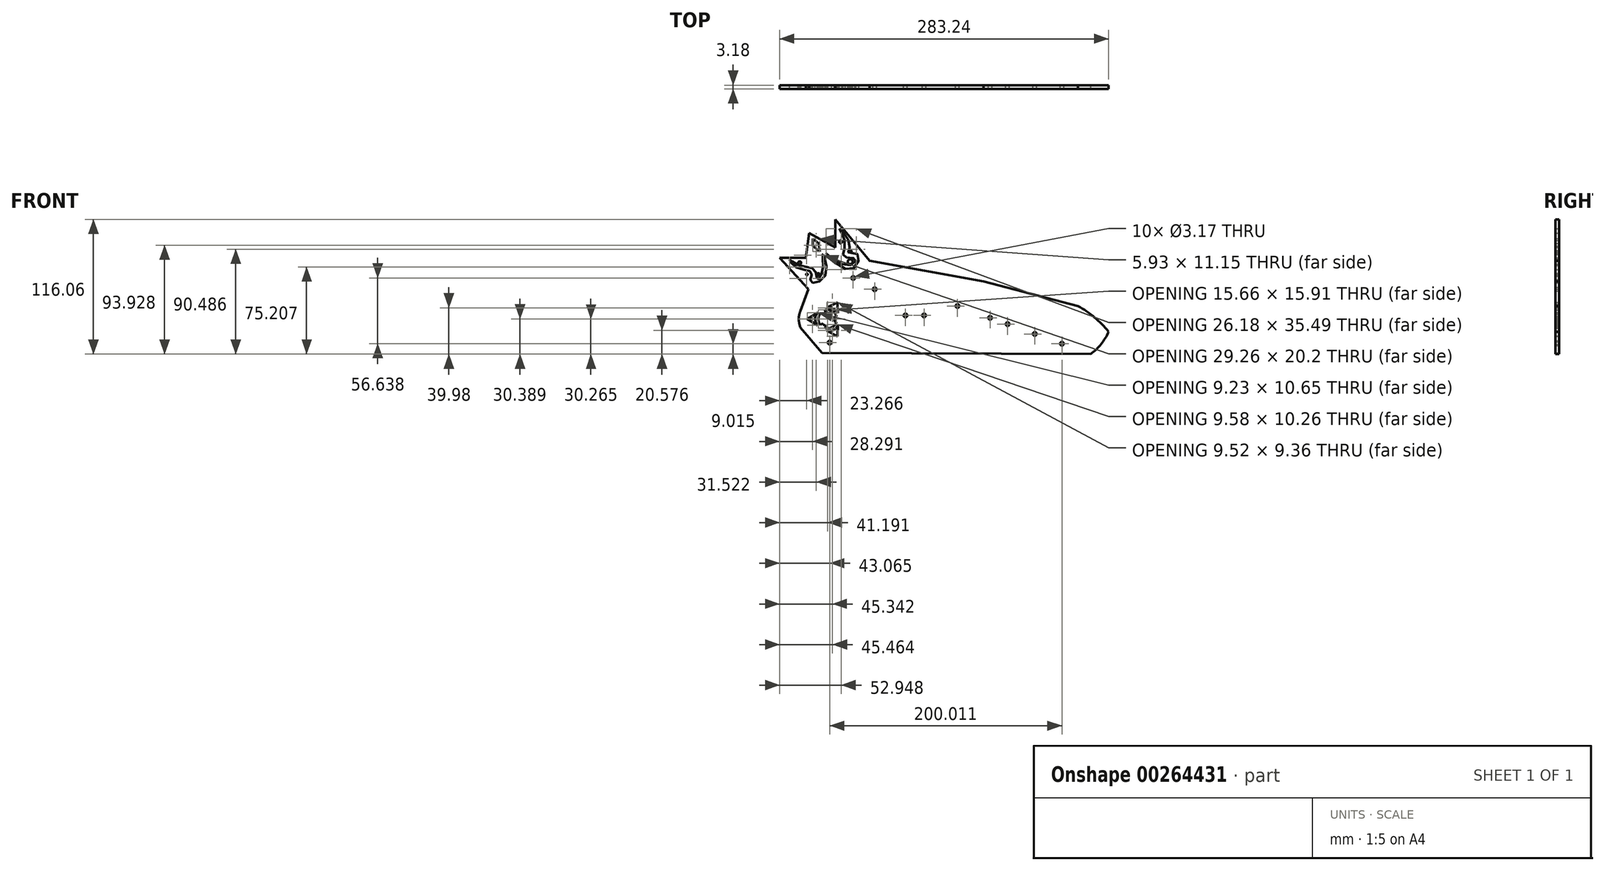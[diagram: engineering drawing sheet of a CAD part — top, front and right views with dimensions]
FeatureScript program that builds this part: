
annotation { "Feature Type Name" : "Feature", "Feature Type Description" : "" }
export const myFeature = defineFeature(function(context is Context, id is Id, definition is map)
    precondition{}
    {
        {
            var Q0;
            Q0=qCreatedBy(makeId("Front.planeOp"),FACE);
            var sketch = newSketch(context, id + "F0", { "sketchPlane" : qUnion([Q0])});
            skCircle(sketch, "E0", {"center": v(-42.49, 14.48) * mm, "radius": 1.59 * mm});
            skCircle(sketch, "E1", {"center": v(-16.03, -8.08) * mm, "radius": 1.59 * mm});
            skLineSegment(sketch, "E2", {"start": v(-99.75, 14.6) * mm, "end": v(-124.36, 41.72) * mm});
            skLineSegment(sketch, "E3", {"start": v(-124.36, 41.72) * mm, "end": v(-101.86, 41.72) * mm});
            skLineSegment(sketch, "E4", {"start": v(-47.04, 39.02) * mm, "end": v(-76.5, 74.6) * mm});
            skLineSegment(sketch, "E5", {"start": v(-76.5, 74.6) * mm, "end": v(-76.5, 50.6) * mm});
            skLineSegment(sketch, "E6", {"start": v(-76.5, 50.6) * mm, "end": v(-98.93, 62.93) * mm});
            skLineSegment(sketch, "E7", {"start": v(-101.86, 41.72) * mm, "end": v(-98.93, 62.93) * mm});
            skPoint(sketch, "E8.visualSharp", {"position": v(-110.59, 3.4) * mm});
            skPoint(sketch, "E9.visualSharp", {"position": v(-87.71, -40.32) * mm});
            skCircle(sketch, "E10", {"center": v(-61.03, 24.2) * mm, "radius": 1.59 * mm});
            skPoint(sketch, "E11.0.midPoint", {"position": v(-90.91, 8.24) * mm});
            skPoint(sketch, "E12.orphan", {"position": v(-121.05, -10.33) * mm});
            skCircle(sketch, "E13", {"center": v(0, -8.08) * mm, "radius": 1.59 * mm});
            skCircle(sketch, "E14", {"center": v(28.76, 0) * mm, "radius": 1.59 * mm});
            skCircle(sketch, "E15", {"center": v(56.86, -10.13) * mm, "radius": 1.59 * mm});
            skCircle(sketch, "E16", {"center": v(71.93, -15.57) * mm, "radius": 1.59 * mm});
            skCircle(sketch, "E17", {"center": v(95.32, -24) * mm, "radius": 1.59 * mm});
            skCircle(sketch, "E18", {"center": v(118.72, -32.44) * mm, "radius": 1.59 * mm});
            skLineSegment(sketch, "E19", {"start": v(143.47, -41.46) * mm, "end": v(-87.71, -40.32) * mm});
            skArc(sketch, "E20", {"start": v(143.47, -41.46) * mm, "mid": v(152.46, -32.83) * mm, "end": v(158.88, -22.16) * mm});
            skArc(sketch, "E21", {"start": v(158.88, -22.16) * mm, "mid": v(146.83, -9.72) * mm, "end": v(132.5, 0) * mm});
            skLineSegment(sketch, "E22", {"start": v(-47.04, 39.02) * mm, "end": v(51.06, 21.22) * mm});
            skLineSegment(sketch, "E23", {"start": v(51.06, 21.22) * mm, "end": v(132.5, 0) * mm});
            skLineSegment(sketch, "E24", {"start": v(-87.71, -40.32) * mm, "end": v(-106.44, -18.45) * mm});
            skLineSegment(sketch, "E25", {"start": v(-106.63, -4.43) * mm, "end": v(-99.75, 14.6) * mm});
            skArc(sketch, "E26", {"start": v(-106.63, -4.43) * mm, "mid": v(-107.82, -11.46) * mm, "end": v(-106.44, -18.45) * mm});
            skLineSegment(sketch, "E27", {"start": v(-89.87, 46.9) * mm, "end": v(-90.77, 53.82) * mm});
            skLineSegment(sketch, "E28", {"start": v(-90.77, 53.82) * mm, "end": v(-95.8, 58.04) * mm});
            skLineSegment(sketch, "E29", {"start": v(-95.8, 58.04) * mm, "end": v(-95.8, 51.75) * mm});
            skLineSegment(sketch, "E30", {"start": v(-95.8, 51.75) * mm, "end": v(-89.87, 46.9) * mm});
            skFitSpline(sketch, "E31", {"points": [v(-115.72, 39.86) * mm, v(-109.85, 33.31) * mm, v(-96.92, 28.78) * mm, v(-97.59, 21.05) * mm, v(-85.33, 25.59) * mm, v(-87.17, 44.57) * mm, v(-87.34, 31.13) * mm, v(-91.88, 23.07) * mm, v(-94.06, 30.8) * mm, v(-109.34, 35.67) * mm, v(-115.72, 39.86) * mm]});
            skFitSpline(sketch, "E32", {"points": [v(-73, 66.77) * mm, v(-63.9, 53.25) * mm, v(-65.05, 45.99) * mm, v(-57.07, 44.37) * mm, v(-63.76, 31.3) * mm, v(-84.6, 45.46) * mm, v(-66.63, 34.87) * mm, v(-58.95, 40.37) * mm, v(-69.16, 42.87) * mm, v(-67.99, 54.65) * mm, v(-73, 66.77) * mm]});
            skCircle(sketch, "E33", {"center": v(-90.9, 27.4) * mm, "radius": 0.97 * mm});
            skCircle(sketch, "E34", {"center": v(-107.1, 37.24) * mm, "radius": 1.3 * mm});
            skCircle(sketch, "E35", {"center": v(-63.58, 38.2) * mm, "radius": 2.08 * mm});
            skCircle(sketch, "E36", {"center": v(-71.9, 55.27) * mm, "radius": 1.22 * mm});
            skCircle(sketch, "E37", {"center": v(-100.85, 27.3) * mm, "radius": 0.76 * mm});
            skCircle(sketch, "E38", {"center": v(-63.19, 47.17) * mm, "radius": 0.78 * mm});
            skPoint(sketch, "E39.0.midPoint", {"position": v(-75.05, -11.2) * mm});
            skPoint(sketch, "E39.cCircle.center.orphan", {"position": v(-83.03, -11.2) * mm});
            skArc(sketch, "E40", {"start": v(-88.94, -5.84) * mm, "mid": v(-91, -11.02) * mm, "end": v(-89.17, -16.28) * mm});
            skArc(sketch, "E41", {"start": v(-83.69, -21.2) * mm, "mid": v(-77.75, -20.5) * mm, "end": v(-74.1, -15.76) * mm});
            skArc(sketch, "E42", {"start": v(-74.26, -6.16) * mm, "mid": v(-78.25, -2.2) * mm, "end": v(-83.78, -1.21) * mm});
            skLineSegment(sketch, "E43", {"start": v(-83.78, -1.21) * mm, "end": v(-74.55, 3.2) * mm});
            skLineSegment(sketch, "E44", {"start": v(-74.26, -6.16) * mm, "end": v(-74.55, 3.2) * mm});
            skLineSegment(sketch, "E45", {"start": v(-83.69, -21.2) * mm, "end": v(-74.43, -26.01) * mm});
            skLineSegment(sketch, "E46", {"start": v(-74.43, -26.01) * mm, "end": v(-74.1, -15.76) * mm});
            skArc(sketch, "E47", {"start": v(-91.46, -5.74) * mm, "mid": v(-93.8, -11.01) * mm, "end": v(-91.74, -16.4) * mm});
            skLineSegment(sketch, "E48", {"start": v(-91.46, -5.74) * mm, "end": v(-100.68, -11.07) * mm});
            skLineSegment(sketch, "E49", {"start": v(-91.74, -16.4) * mm, "end": v(-100.68, -11.07) * mm});
            skPoint(sketch, "E50.orphan", {"position": v(-73.54, 5.24) * mm});
            skPoint(sketch, "E39.0.end.orphan", {"position": v(-76.56, -27.62) * mm});
            skCircle(sketch, "E51", {"center": v(-83.03, -11.2) * mm, "radius": 6.01 * mm});
            skLineSegment(sketch, "E52", {"start": v(-83.03, -11.2) * mm, "end": v(-89.17, -16.28) * mm});
            skLineSegment(sketch, "E53", {"start": v(-83.03, -11.2) * mm, "end": v(-85.05, -18.9) * mm});
            skLineSegment(sketch, "E54", {"start": v(-83.03, -11.2) * mm, "end": v(-88.94, -5.84) * mm});
            skLineSegment(sketch, "E55", {"start": v(-83.03, -11.2) * mm, "end": v(-85.15, -3.5) * mm});
            skLineSegment(sketch, "E56", {"start": v(-83.03, -11.2) * mm, "end": v(-75.34, -9.07) * mm});
            skLineSegment(sketch, "E57", {"start": v(-83.03, -11.2) * mm, "end": v(-75.48, -13.78) * mm});
            skArc(sketch, "E58.trimOffspring", {"start": v(-75.34, -9.07) * mm, "mid": v(-79.1, -4.25) * mm, "end": v(-85.15, -3.5) * mm});
            skArc(sketch, "E59.trimOffspring", {"start": v(-85.05, -18.9) * mm, "mid": v(-79.26, -18.22) * mm, "end": v(-75.48, -13.78) * mm});
            skLineSegment(sketch, "E60", {"start": v(-107.82, -10.33) * mm, "end": v(-107.82, -56.76) * mm});
            skPoint(sketch, "E60.startSnap0", {"position": v(-107.82, -11.46) * mm});
            skLineSegment(sketch, "E61", {"start": v(158.88, -22.16) * mm, "end": v(158.88, -59.21) * mm});
            skPoint(sketch, "E62.start.orphan", {"position": v(-107.82, -40.32) * mm});
            skCircle(sketch, "E63", {"center": v(-81.3, -31.46) * mm, "radius": 1.59 * mm});
            skSolve(sketch);
        }
        {
            var Q0;
            Q0=makeQuery(id+"F0.imprint","IMPRINT",FACE,{"disambiguationData":[TD([[makeQuery(id+"F0.imprint","IMPRINT",EDGE,{"derivedFrom":sQuery(id+"F0.wireOp",EDGE,"E0")}),-1.0]])]});
            extrude(context, id + "F1", {"entities" : qUnion([Q0]), "depth" : 3.17 * mm});
        }
    });
